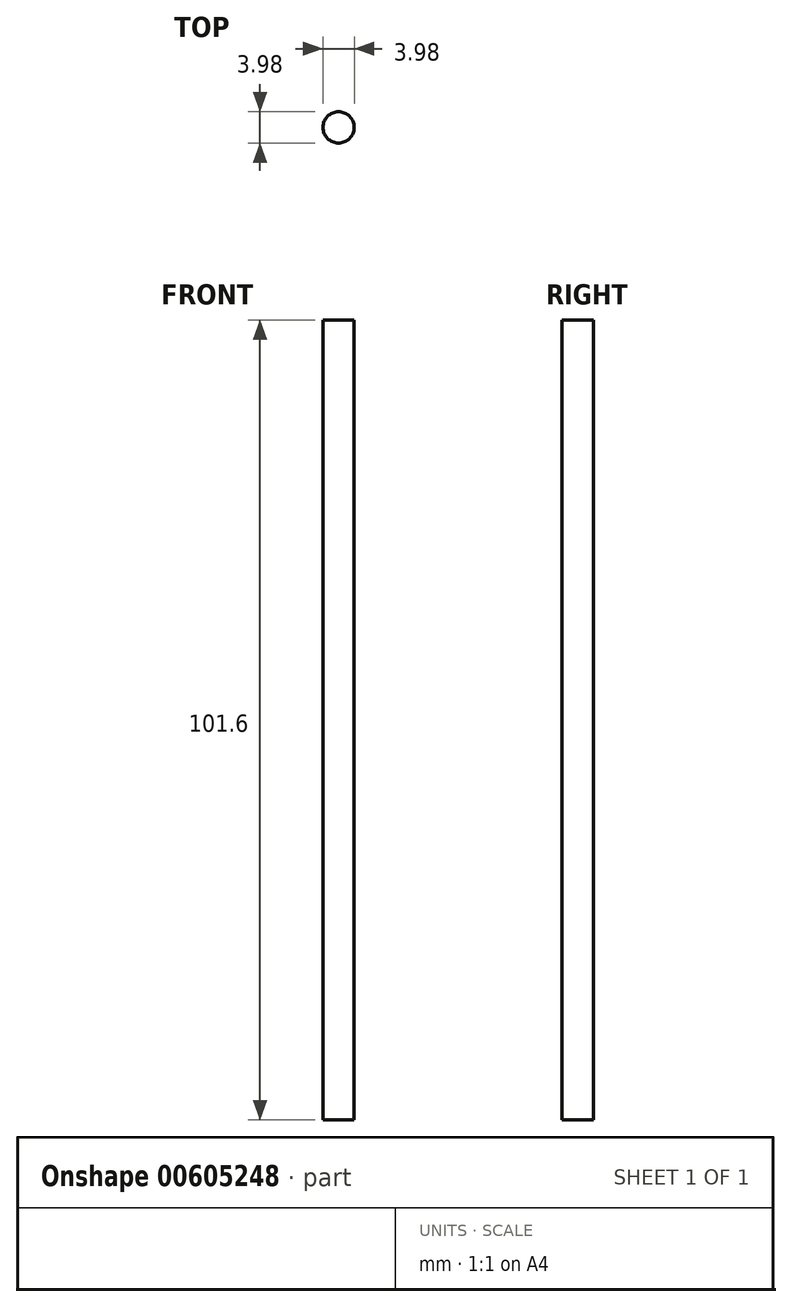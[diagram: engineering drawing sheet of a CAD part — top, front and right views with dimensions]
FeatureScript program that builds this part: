
annotation { "Feature Type Name" : "Feature", "Feature Type Description" : "" }
export const myFeature = defineFeature(function(context is Context, id is Id, definition is map)
    precondition{}
    {
        {
            var Q0;
            Q0=qCreatedBy(makeId("Top.planeOp"),FACE);
            var sketch = newSketch(context, id + "F0", { "sketchPlane" : qUnion([Q0])});
            skCircle(sketch, "E0", {"center": v(0, 0) * mm, "radius": 1.99 * mm});
            skSolve(sketch);
        }
        {
            var Q0;
            Q0 = qSketchRegion(id + "F0", true);
            extrude(context, id + "F1", {"entities" : qUnion([Q0]), "depth" : 101.6 * mm, "offsetDistance" : 25.4 * mm});
        }
    });
